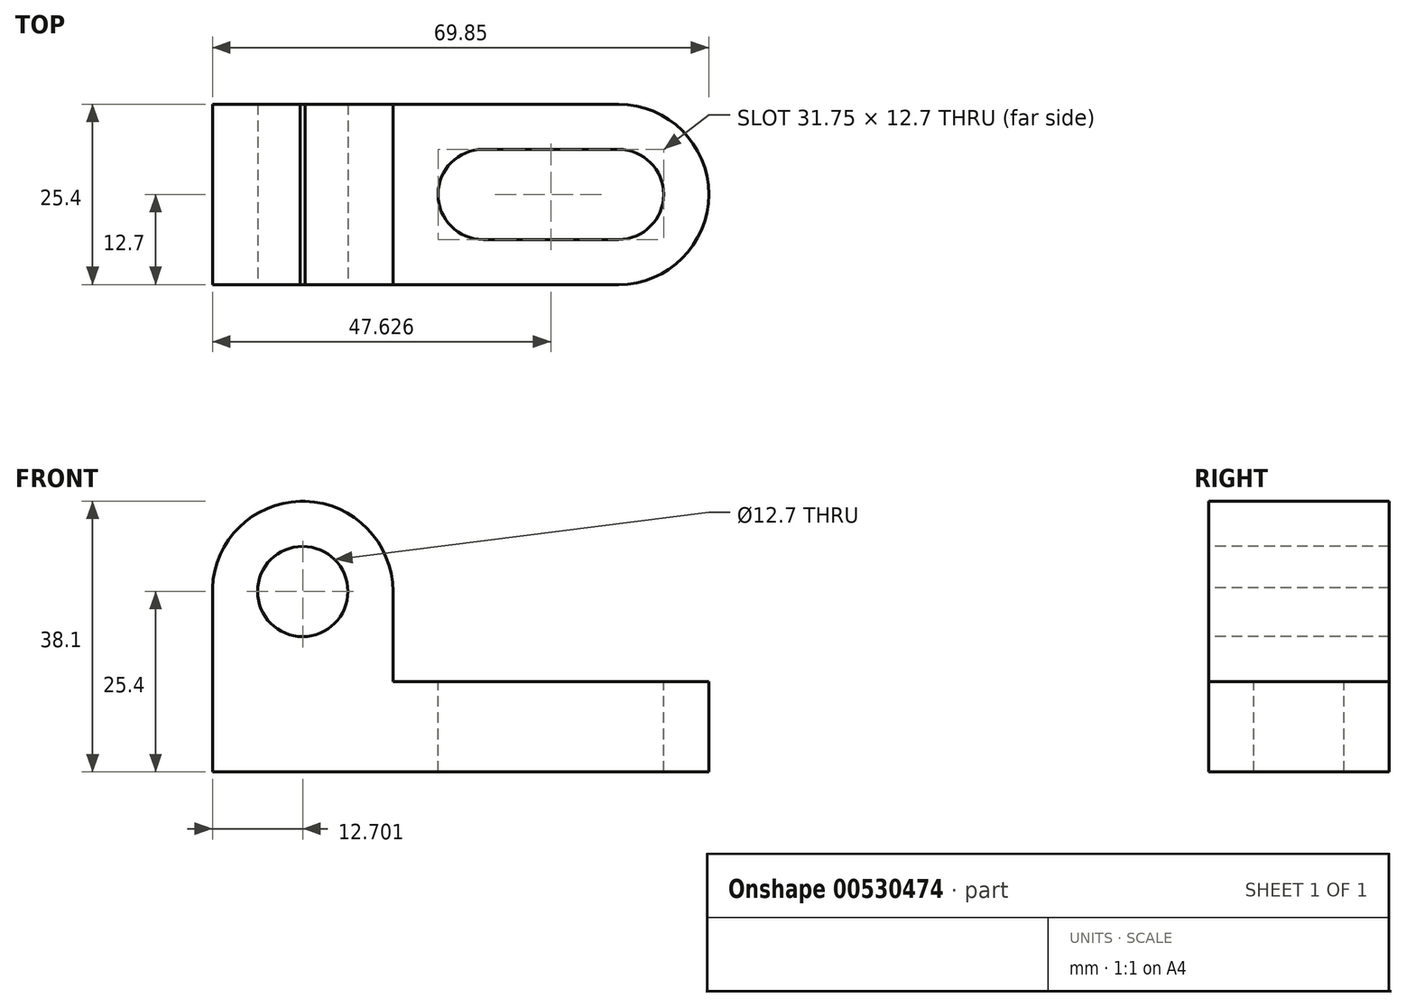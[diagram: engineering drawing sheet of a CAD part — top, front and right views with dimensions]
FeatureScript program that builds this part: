
annotation { "Feature Type Name" : "Feature", "Feature Type Description" : "" }
export const myFeature = defineFeature(function(context is Context, id is Id, definition is map)
    precondition{}
    {
        {
            var Q0;
            Q0=qCreatedBy(makeId("Front.planeOp"),FACE);
            var sketch = newSketch(context, id + "F0", { "sketchPlane" : qUnion([Q0])});
            skLineSegment(sketch, "E0", {"start": v(-73.46, 0) * mm, "end": v(-3.6, 0) * mm});
            skLineSegment(sketch, "E1", {"start": v(-3.6, 0) * mm, "end": v(-3.6, 12.7) * mm});
            skLineSegment(sketch, "E2", {"start": v(-3.6, 12.7) * mm, "end": v(-48.06, 12.7) * mm});
            skLineSegment(sketch, "E3", {"start": v(-73.46, 0) * mm, "end": v(-73.46, 38.1) * mm});
            skLineSegment(sketch, "E4", {"start": v(-48.06, 12.7) * mm, "end": v(-48.06, 38.1) * mm});
            skLineSegment(sketch, "E5", {"start": v(-48.06, 38.1) * mm, "end": v(-73.46, 38.1) * mm});
            skSolve(sketch);
        }
        {
            var Q0;
            Q0=makeQuery(id+"F0.imprint","IMPRINT",FACE,{"disambiguationData":[TD([[makeQuery(id+"F0.imprint","IMPRINT",EDGE,{"derivedFrom":sQuery(id+"F0.wireOp",EDGE,"E0")}),1.0]])]});
            extrude(context, id + "F1", {"entities" : qUnion([Q0]), "depth" : 25.4 * mm, "offsetDistance" : 25.4 * mm});
        }
        {
            var Q0;
            Q0=makeQuery(id+"F1.opExtrude","CAP_FACE",FACE,{"disambiguationData":[OSD([sQuery(id+"F0.wireOp",EDGE,"E0"),sQuery(id+"F0.wireOp",EDGE,"E1"),sQuery(id+"F0.wireOp",EDGE,"E2"),sQuery(id+"F0.wireOp",EDGE,"E3"),sQuery(id+"F0.wireOp",EDGE,"E4"),sQuery(id+"F0.wireOp",EDGE,"E5")])],"isStart":false});
            var sketch = newSketch(context, id + "F2", { "sketchPlane" : qUnion([Q0])});
            skCircle(sketch, "E6", {"center": v(-60.76, 25.4) * mm, "radius": 6.35 * mm});
            skArc(sketch, "E7", {"start": v(-48.06, 25.4) * mm, "mid": v(-60.51, 38.1) * mm, "end": v(-73.46, 25.9) * mm});
            skSolve(sketch);
        }
        {
            var Q0;
            Q0 = qSketchRegion(id + "F2", true);
            var Q1;
            {var subQ0=sQuery(id+"F2.wireOp",EDGE,"E7");var subQ1=makeQuery(id+"F1.opExtrude","CAP_EDGE",EDGE,{"disambiguationData":[OSD([sQuery(id+"F0.wireOp",EDGE,"E3")])],"isStart":false});var subQ2=makeQuery(id+"F2.imprint","INTERSECT",VERTEX,{"derivedFrom":[subQ1,subQ0]});Q1=makeQuery(id+"F2.imprint","IMPRINT",FACE,{"disambiguationData":[TD([[makeQuery(id+"F2.imprint","IMPRINT",EDGE,{"disambiguationData":[TD([[subQ2,1.0]])],"derivedFrom":subQ0}),-1.0]])]});}
            var Q2;
            {var subQ0=sQuery(id+"F2.wireOp",EDGE,"E7");var subQ1=makeQuery(id+"F1.opExtrude","CAP_EDGE",EDGE,{"disambiguationData":[OSD([sQuery(id+"F0.wireOp",EDGE,"E4")])],"isStart":false});var subQ2=makeQuery(id+"F2.imprint","INTERSECT",VERTEX,{"derivedFrom":[subQ1,subQ0]});Q2=makeQuery(id+"F2.imprint","IMPRINT",FACE,{"disambiguationData":[TD([[makeQuery(id+"F2.imprint","IMPRINT",EDGE,{"disambiguationData":[TD([[subQ2,-1.0]])],"derivedFrom":subQ0}),-1.0]])]});}
            extrude(context, id + "F3", {"entities" : qUnion([Q0, Q1, Q2]), "operationType" : NewBodyOperationType.REMOVE, "oppositeDirection" : true, "depth" : 25.4 * mm, "offsetDistance" : 25.4 * mm});
        }
        {
            var Q0;
            Q0=makeQuery(id+"F1.opExtrude","SWEPT_FACE",FACE,{"disambiguationData":[OSD([sQuery(id+"F0.wireOp",EDGE,"E2")])]});
            var sketch = newSketch(context, id + "F4", { "sketchPlane" : qUnion([Q0])});
            skCircle(sketch, "E8", {"center": v(-16.3, -12.7) * mm, "radius": 6.35 * mm});
            skCircle(sketch, "E9", {"center": v(-35.36, -12.7) * mm, "radius": 6.35 * mm});
            skArc(sketch, "E10", {"start": v(-16.3, -25.4) * mm, "mid": v(-3.6, -12.7) * mm, "end": v(-16.3, 0) * mm});
            skLineSegment(sketch, "E11", {"start": v(-35.36, -19.05) * mm, "end": v(-16.3, -19.05) * mm});
            skLineSegment(sketch, "E12", {"start": v(-35.36, -6.35) * mm, "end": v(-16.3, -6.35) * mm});
            skSolve(sketch);
        }
        {
            var Q0;
            Q0 = qSketchRegion(id + "F4", true);
            var Q1;
            {var subQ0=sQuery(id+"F4.wireOp",EDGE,"E10");var subQ1=sQuery(id+"F0.wireOp",EDGE,"E2");var subQ2=makeQuery(id+"F1.opExtrude","CAP_EDGE",EDGE,{"disambiguationData":[OSD([subQ1])],"isStart":false});var subQ3=makeQuery(id+"F4.imprint","INTERSECT",VERTEX,{"derivedFrom":[subQ2,subQ0]});Q1=makeQuery(id+"F4.imprint","IMPRINT",FACE,{"disambiguationData":[TD([[makeQuery(id+"F4.imprint","IMPRINT",EDGE,{"disambiguationData":[TD([[subQ3,-1.0]])],"derivedFrom":subQ0}),-1.0]])]});}
            var Q2;
            {var subQ0=sQuery(id+"F4.wireOp",EDGE,"E10");var subQ1=sQuery(id+"F0.wireOp",EDGE,"E2");var subQ2=makeQuery(id+"F1.opExtrude","CAP_EDGE",EDGE,{"disambiguationData":[OSD([subQ1])],"isStart":true});var subQ3=makeQuery(id+"F4.imprint","INTERSECT",VERTEX,{"derivedFrom":[subQ2,subQ0]});Q2=makeQuery(id+"F4.imprint","IMPRINT",FACE,{"disambiguationData":[TD([[makeQuery(id+"F4.imprint","IMPRINT",EDGE,{"disambiguationData":[TD([[subQ3,1.0]])],"derivedFrom":subQ0}),-1.0]])]});}
            extrude(context, id + "F5", {"entities" : qUnion([Q0, Q1, Q2]), "operationType" : NewBodyOperationType.REMOVE, "endBound" : BoundingType.THROUGH_ALL, "oppositeDirection" : true, "depth" : 25.4 * mm, "offsetDistance" : 25.4 * mm});
        }
    });
